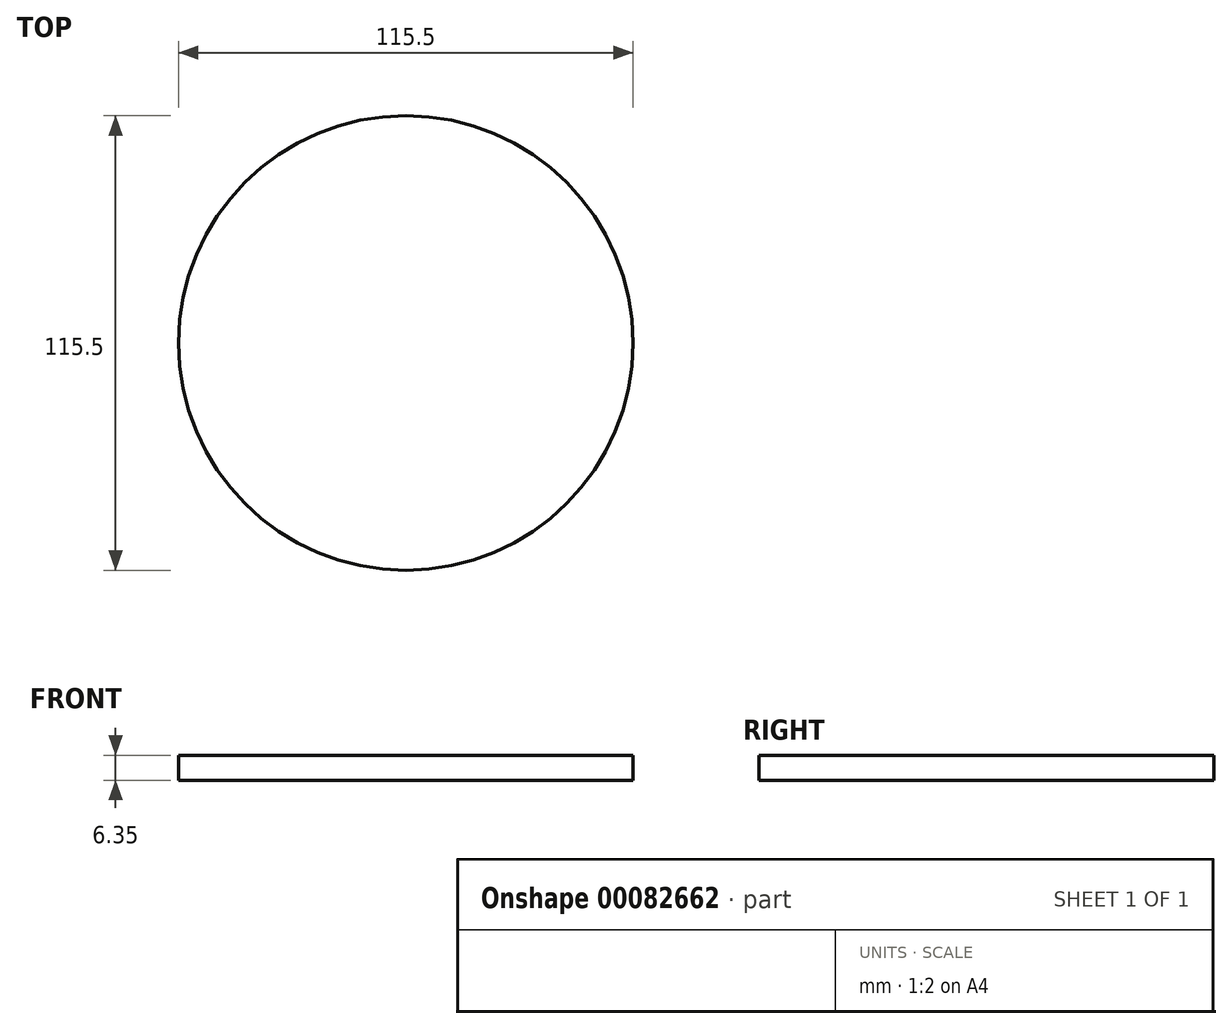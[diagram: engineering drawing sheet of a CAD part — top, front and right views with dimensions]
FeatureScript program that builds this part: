
annotation { "Feature Type Name" : "Feature", "Feature Type Description" : "" }
export const myFeature = defineFeature(function(context is Context, id is Id, definition is map)
    precondition{}
    {
        {
            var Q0;
            Q0=qCreatedBy(makeId("Top.planeOp"),FACE);
            var sketch = newSketch(context, id + "F0", { "sketchPlane" : qUnion([Q0])});
            skCircle(sketch, "E0", {"center": v(0, 0) * mm, "radius": 57.75 * mm});
            skSolve(sketch);
        }
        {
            var Q0;
            Q0 = qSketchRegion(id + "F0", true);
            extrude(context, id + "F1", {"entities" : qUnion([Q0]), "depth" : 6.35 * mm});
        }
    });
